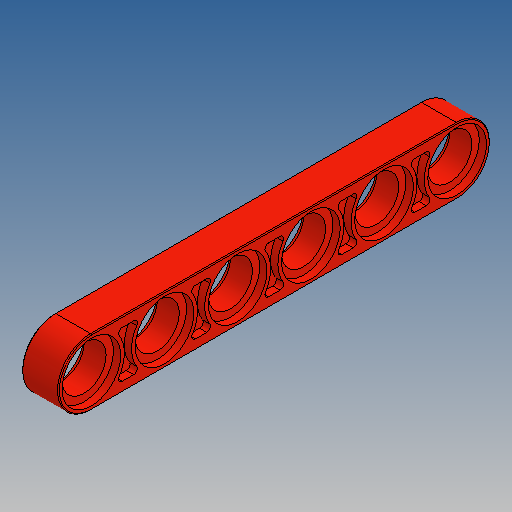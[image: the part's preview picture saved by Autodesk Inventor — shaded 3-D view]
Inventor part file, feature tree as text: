
AUTODESK INVENTOR PART (.ipt)
format: ipt  version: 2025 (Build 290162010, 162A)  size: 331,776 bytes
history: native  units: mm
features: extrude x3, sketch x3, mirror x1, fillet x1
ambient origin geometry x8: Origin, YZ Plane, XZ Plane, XY Plane, X Axis, Y Axis, Z Axis, Center Point
bodies: Solid1 (feature_tree)
feature tree (8):
  extrude  "Extrusion4"  Depth=7.2mm
  sketch  "Sketch11"  dims[d60=4.8mm d61=6.4mm d62=0.8mm d63=0.0mm d64=8.0mm d65=45.0deg d66=50.0mm d68=8.0mm d69=10.0mm d71=10.0mm d73=0.8mm d74=0.0mm d75=0.4mm]
  extrude  "Extrusion16"  Depth=0.1mm
  extrude  "Extrusion17"  Depth=0.4mm
  mirror  "Mirror3"
  fillet  "Fillet1"  Radius=0.8mm
  sketch  "Sketch3"  dims[d56=0.1mm d59=6.4mm]
  sketch  "Skizze - Rechteckige Anordnung1"  dims[d15=4.0mm d16=0.0mm d49=7.2mm]
